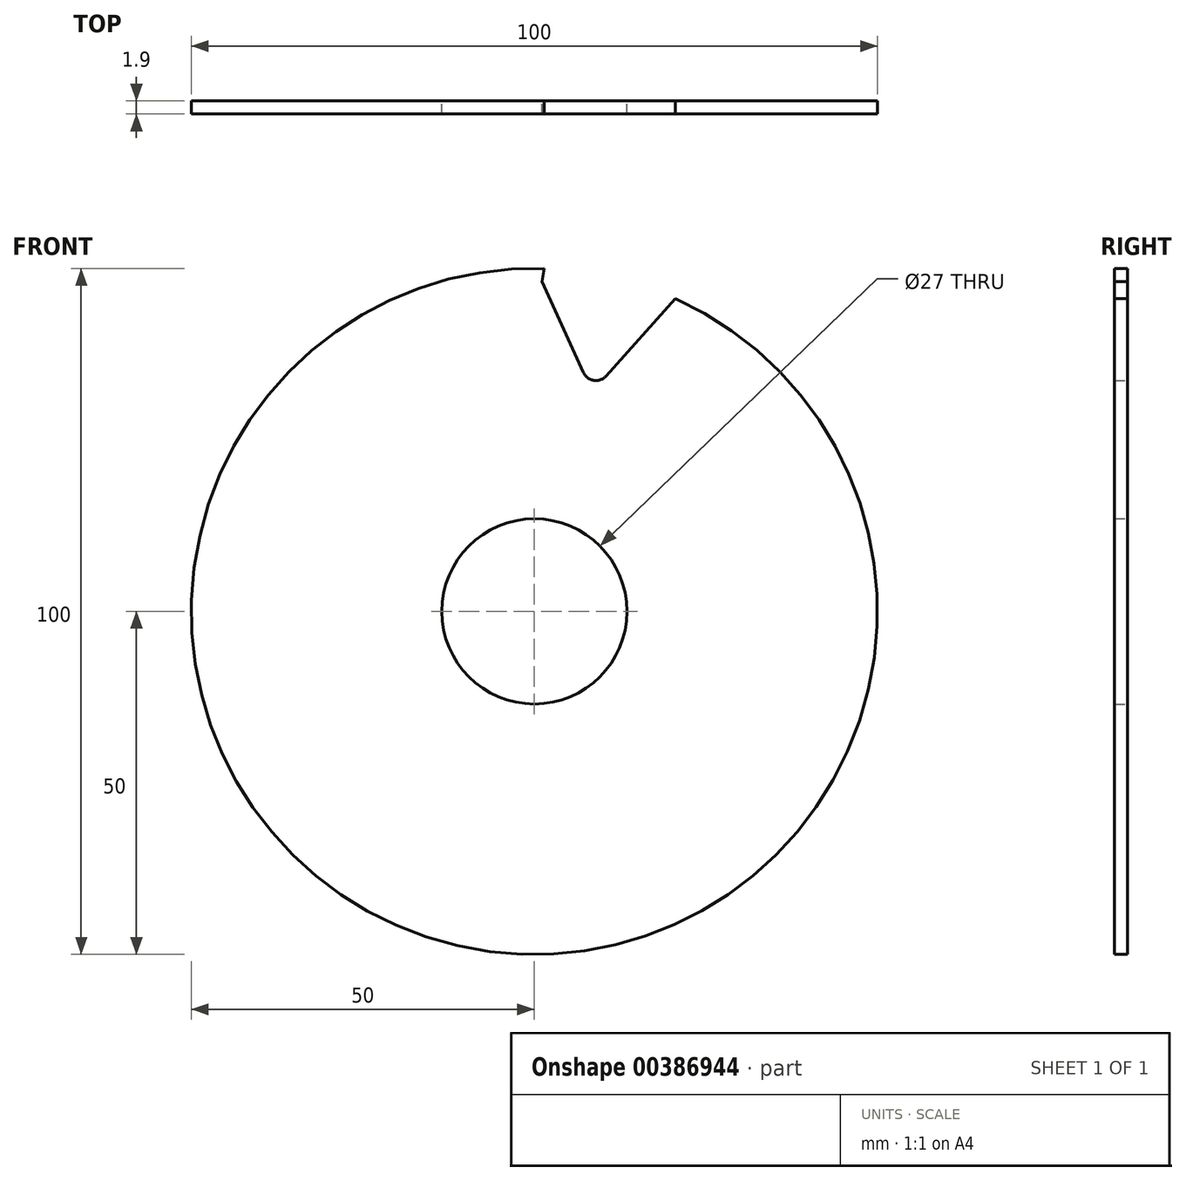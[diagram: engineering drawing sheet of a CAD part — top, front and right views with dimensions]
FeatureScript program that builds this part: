
annotation { "Feature Type Name" : "Feature", "Feature Type Description" : "" }
export const myFeature = defineFeature(function(context is Context, id is Id, definition is map)
    precondition{}
    {
        {
            var Q0;
            Q0=qCreatedBy(makeId("Front.planeOp"),FACE);
            var sketch = newSketch(context, id + "F0", { "sketchPlane" : qUnion([Q0])});
            skCircle(sketch, "E0", {"center": v(0, 0) * mm, "radius": 50 * mm});
            skCircle(sketch, "E1", {"center": v(0, 0) * mm, "radius": 13.5 * mm});
            skSolve(sketch);
        }
        {
            var Q0;
            Q0 = qSketchRegion(id + "F0", true);
            extrude(context, id + "F1", {"entities" : qUnion([Q0]), "depth" : 1.9 * mm});
        }
        {
            var Q0;
            Q0=qCreatedBy(makeId("Front.planeOp"),FACE);
            var sketch = newSketch(context, id + "F2", { "sketchPlane" : qUnion([Q0])});
            skLineSegment(sketch, "E2", {"start": v(0, 50.2) * mm, "end": v(2.73, 35.82) * mm});
            skLineSegment(sketch, "E3", {"start": v(5.84, 34.56) * mm, "end": v(21.02, 45.13) * mm});
            skLineSegment(sketch, "E4", {"start": v(21.02, 45.13) * mm, "end": v(12.48, 60.96) * mm});
            skLineSegment(sketch, "E5", {"start": v(12.48, 60.96) * mm, "end": v(0, 50.2) * mm});
            skPoint(sketch, "E6.visualSharp", {"position": v(3.3, 32.8) * mm});
            skArc(sketch, "E6.filletArc", {"start": v(2.73, 35.82) * mm, "mid": v(3.94, 34.34) * mm, "end": v(5.84, 34.56) * mm});
            skSolve(sketch);
        }
        {
            var Q0;
            Q0 = qSketchRegion(id + "F2", true);
            extrude(context, id + "F3", {"entities" : qUnion([Q0]), "operationType" : NewBodyOperationType.REMOVE, "oppositeDirection" : true, "depth" : 25 * mm});
        }
        {
            var Q0;
            Q0=qCreatedBy(makeId("Front.planeOp"),FACE);
            var sketch = newSketch(context, id + "F4", { "sketchPlane" : qUnion([Q0])});
            skLineSegment(sketch, "E7", {"start": v(22.71, 48.03) * mm, "end": v(18.25, 59.06) * mm});
            skLineSegment(sketch, "E8", {"start": v(18.25, 59.06) * mm, "end": v(1.7, 51.28) * mm});
            skPoint(sketch, "E9.visualSharp", {"position": v(0, 31.42) * mm});
            skLineSegment(sketch, "E10", {"start": v(1.1, 48.08) * mm, "end": v(7.14, 34.82) * mm});
            skLineSegment(sketch, "E11", {"start": v(10.45, 34.32) * mm, "end": v(22.71, 48.03) * mm});
            skPoint(sketch, "E12.visualSharp", {"position": v(8.41, 32.03) * mm});
            skArc(sketch, "E12.filletArc", {"start": v(7.14, 34.82) * mm, "mid": v(8.66, 33.67) * mm, "end": v(10.45, 34.32) * mm});
            skLineSegment(sketch, "E13", {"start": v(1.1, 48.08) * mm, "end": v(1.7, 51.28) * mm});
            skPoint(sketch, "E14.orphan", {"position": v(0, 50.48) * mm});
            skSolve(sketch);
        }
        {
            var Q0;
            Q0 = qSketchRegion(id + "F4", true);
            extrude(context, id + "F5", {"entities" : qUnion([Q0]), "operationType" : NewBodyOperationType.REMOVE, "depth" : 25 * mm});
        }
    });
